# Revit family: RN 11013 Réducteur de pression sans raccords
name_source: partatom
category: Rohrzubehör
units: mm (PartAtom-declared; Revit-internal decimal feet)

## family parameters
Arbeitsebenenbasiert = Nein
Beim Laden mit Abzugskörper schneiden = Nein
Bemaßung runder Anschluss = Durchmesser verwenden
Gemeinsam genutzt = Nein
Immer vertikal = Ja
Teiletyp = Ventil - Zerlegung in

## types (6) — shared parameters
1.010.00.2 Blattnummer der Richtlinie = 17
1.010.00.3 Ausgabedatum (Monat) der Richtlinie = 201601
1.010.00.4 Herstellername = R. Nussbaum AG
1.010.00.5 Revisionsdatum der Datei = 20190528
1.010.00.6 Webadresse des Herstellers = http://www.nussbaum.ch
1.100.00.3 Sortiernummer für Anzeigereihenfolge = 8
1.100.00.4 Produktbezeichnung = Druckminderer
1.960/3L.00.8 Link (URL) = https://www.nussbaum.ch
17.700.00.4 Armaturentyp = 8
17.700.00.7 Maximale Betriebstemperatur TB [°C] = 80
17.700.00.8 Maximaler Betriebsdruck (Arbeitsdruck) ps [1.0 · 105 Pa] = 16
Connector Visibility = Nein
EnclosingSpace Visibility = Nein
Hersteller = R. Nussbauzm AG
URL = https://www.nussbaum.ch

## per-type parameters (varying)
| type | 1.800.00.3 TGA-Nummer | 1.810.00.3 Hersteller-Bestellnummer | 1.810.00.4 DATANORM-Nummer | 1.810.00.6 GTIN-Nummer | 17.700.00.30 Produktbeschreibung | 17.700.00.5 Nennweite DN | 17.700.00.6 kvs-Wert [m3/h] | CONNECTOR0_DIAMETER_dX_0r | CONNECTOR0_dX_00 | CONNECTOR0_dX_01 | CONNECTOR0_ref_dX | CONNECTOR1_DIAMETER_dX_0r | CONNECTOR1_dX_00 | CONNECTOR1_dX_01 | CONNECTOR1_ref_dX | Modell | R. Nussbaum AG 11013.34 de Visibility | R. Nussbaum AG 11013.35 de Visibility | R. Nussbaum AG 11013.36 de Visibility | R. Nussbaum AG 11013.37 de Visibility | R. Nussbaum AG 11013.38 de Visibility | R. Nussbaum AG 11013.39 de Visibility | Typenkommentare |
| DN 15 | 00800400000000000000000000000200700000000000000001???00000 | 11013.34 | 11013.34 | 7612945712356 | 11013.34, Druckreduzierventil ohne Verschraubungen, Einstellbereich 1 bis 5 bar, | 15 | 3.48 | 15 mm  [stored 0.0492126 ft] | 40 mm | 31 mm | 40 mm | 15 mm  [stored 0.0492126 ft] | 31 mm | 40 mm | 40 mm | 11013.34 | Ja | Nein | Nein | Nein | Nein | Nein | Réducteur de pression sans raccordsDN 15 |
| DN 20 | 00800400000000000000000000000200700000000000000002???00000 | 11013.35 | 11013.35 | 7612945712394 | 11013.35, Druckreduzierventil ohne Verschraubungen, Einstellbereich 1 bis 5 bar, | 20 | 4.5 | 20 mm  [stored 0.0656168 ft] | 43 mm | 34 mm | 43 mm | 20 mm  [stored 0.0656168 ft] | 34 mm | 43 mm | 43 mm | 11013.35 | Nein | Ja | Nein | Nein | Nein | Nein | Réducteur de pression sans raccordsDN 20 |
| DN 25 | 00800400000000000000000000000200700000000000000003???00000 | 11013.36 | 11013.36 | 7612945712431 | 11013.36, Druckreduzierventil ohne Verschraubungen, Einstellbereich 1 bis 5 bar, | 25 | 5.52 | 25 mm  [stored 0.082021 ft] | 50 mm  [stored 0.164042 ft] | 38 mm | 50 mm  [stored 0.164042 ft] | 25 mm  [stored 0.082021 ft] | 38 mm | 50 mm  [stored 0.164042 ft] | 50 mm  [stored 0.164042 ft] | 11013.36 | Nein | Nein | Ja | Nein | Nein | Nein | Réducteur de pression sans raccordsDN 25 |
| DN 32 | 00800400000000000000000000000200700000000000000004???00000 | 11013.37 | 11013.37 | 7612945711861 | 11013.37, Druckreduzierventil ohne Verschraubungen, Einstellbereich 1 bis 5 bar, | 32 | 13.2 | 32 mm  [stored 0.104987 ft] | 60 mm | 47 mm | 60 mm | 32 mm  [stored 0.104987 ft] | 47 mm | 60 mm | 60 mm | 11013.37 | Nein | Nein | Nein | Ja | Nein | Nein | Réducteur de pression sans raccordsDN 32 |
| DN 40 | 00800400000000000000000000000200700000000000000005???00000 | 11013.38 | 11013.38 | 7612945712103 | 11013.38, Druckreduzierventil ohne Verschraubungen, Einstellbereich 1 bis 5 bar, | 40 | 16.2 | 40 mm | 73 mm | 59 mm | 73 mm | 40 mm | 59 mm | 73 mm | 73 mm | 11013.38 | Nein | Nein | Nein | Nein | Ja | Nein | Réducteur de pression sans raccordsDN 40 |
| DN 50 | 00800400000000000000000000000200700000000000000006???00000 | 11013.39 | 11013.39 | 7612945712141 | 11013.39, Druckreduzierventil ohne Verschraubungen, Einstellbereich 1 bis 5 bar, | 50 | 21.6 | 50 mm  [stored 0.164042 ft] | 88 mm | 71 mm | 88 mm | 50 mm  [stored 0.164042 ft] | 71 mm | 88 mm | 88 mm | 11013.39 | Nein | Nein | Nein | Nein | Nein | Ja | Réducteur de pression sans raccordsDN 50 |

note: [stored X ft] marks values corroborated as IEEE doubles in the binary element streams (Revit-internal decimal feet)
